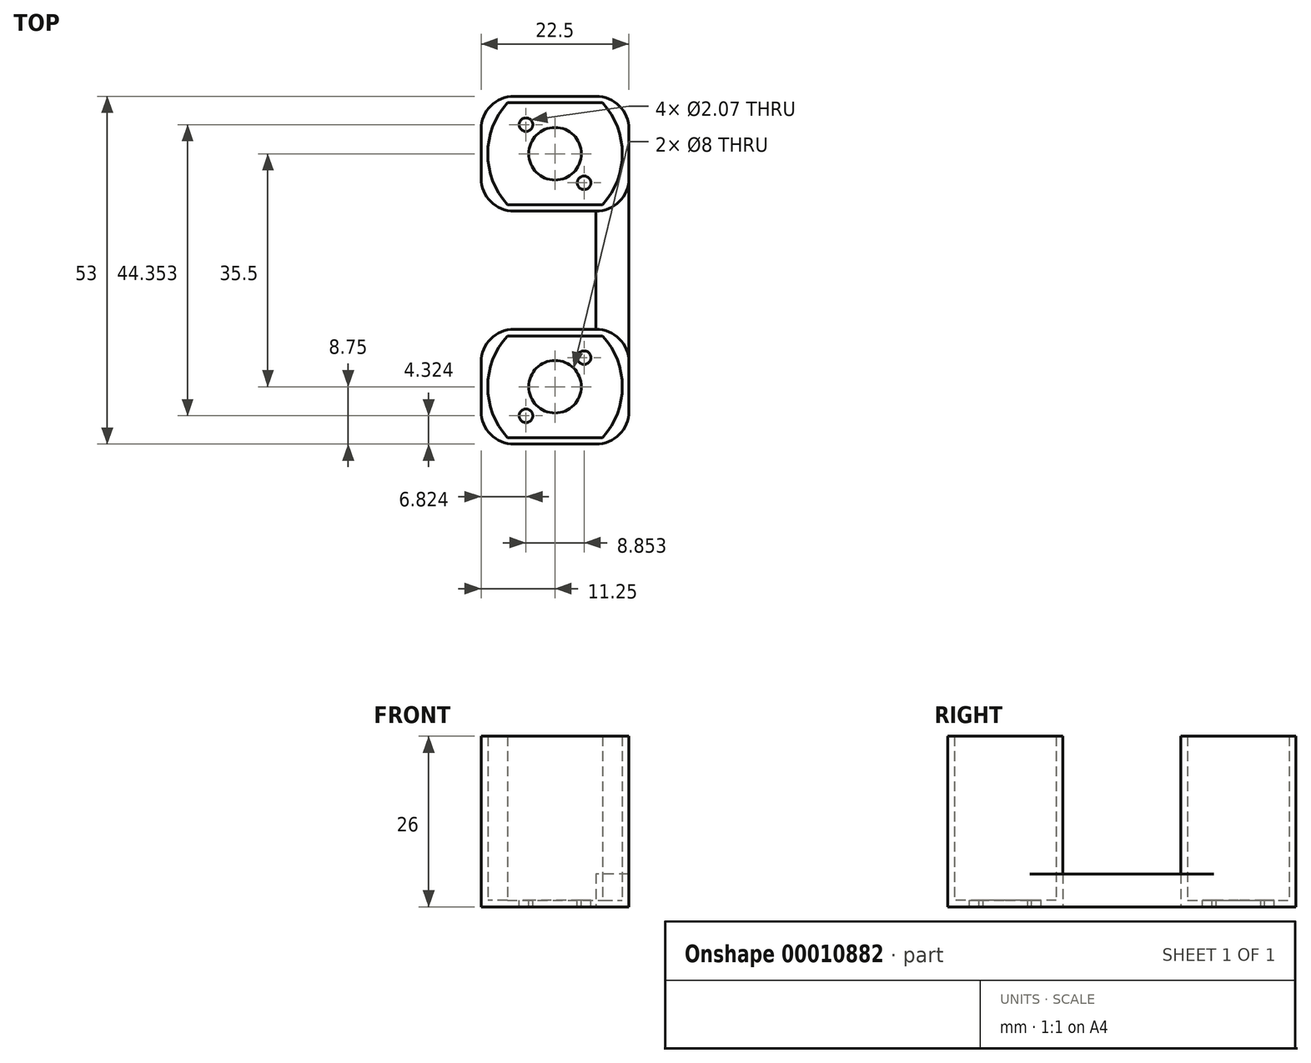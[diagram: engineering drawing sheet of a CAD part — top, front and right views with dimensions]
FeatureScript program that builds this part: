
annotation { "Feature Type Name" : "Feature", "Feature Type Description" : "" }
export const myFeature = defineFeature(function(context is Context, id is Id, definition is map)
    precondition{}
    {
        {
            var Q0;
            Q0=qCreatedBy(makeId("Top.planeOp"),FACE);
            var sketch = newSketch(context, id + "F0", { "sketchPlane" : qUnion([Q0])});
            skLineSegment(sketch, "E0.bottom", {"start": v(-7.25, 7.75) * mm, "end": v(7.25, 7.75) * mm});
            skLineSegment(sketch, "E0.top", {"start": v(-7.25, -7.75) * mm, "end": v(7.25, -7.75) * mm});
            skLineSegment(sketch, "E0.left", {"start": v(-7.25, 7.75) * mm, "end": v(-7.25, -7.75) * mm, "construction": true});
            skLineSegment(sketch, "E0.right", {"start": v(7.25, 7.75) * mm, "end": v(7.25, -7.75) * mm, "construction": true});
            skArc(sketch, "E1", {"start": v(-7.25, 7.75) * mm, "mid": v(-10.25, 0) * mm, "end": v(-7.25, -7.75) * mm});
            skArc(sketch, "E2", {"start": v(7.25, -7.75) * mm, "mid": v(10.25, 0) * mm, "end": v(7.25, 7.75) * mm});
            skLineSegment(sketch, "E3", {"start": v(-7.25, 7.75) * mm, "end": v(-10.25, 7.75) * mm, "construction": true});
            skLineSegment(sketch, "E4", {"start": v(-10.25, 7.75) * mm, "end": v(-10.25, -7.75) * mm, "construction": true});
            skLineSegment(sketch, "E5", {"start": v(-10.25, -7.75) * mm, "end": v(-7.25, -7.75) * mm, "construction": true});
            skLineSegment(sketch, "E6", {"start": v(7.25, -7.75) * mm, "end": v(10.25, -7.75) * mm, "construction": true});
            skLineSegment(sketch, "E7", {"start": v(10.25, -7.75) * mm, "end": v(10.25, 7.75) * mm, "construction": true});
            skLineSegment(sketch, "E8", {"start": v(10.25, 7.75) * mm, "end": v(7.25, 7.75) * mm, "construction": true});
            skLineSegment(sketch, "E9.bottom", {"start": v(-11.25, 8.75) * mm, "end": v(11.25, 8.75) * mm});
            skLineSegment(sketch, "E9.top", {"start": v(-11.25, -8.75) * mm, "end": v(11.25, -8.75) * mm});
            skLineSegment(sketch, "E9.left", {"start": v(-11.25, 8.75) * mm, "end": v(-11.25, -8.75) * mm});
            skLineSegment(sketch, "E9.right", {"start": v(11.25, 8.75) * mm, "end": v(11.25, -8.75) * mm});
            skPoint(sketch, "E10.visualSharp", {"position": v(-11.25, 8.75) * mm});
            skPoint(sketch, "E11.visualSharp", {"position": v(11.25, 8.75) * mm});
            skPoint(sketch, "E12.visualSharp", {"position": v(11.25, -8.75) * mm});
            skPoint(sketch, "E13.visualSharp", {"position": v(-11.25, -8.75) * mm});
            skLineSegment(sketch, "E14", {"start": v(-1.26, 0) * mm, "end": v(1.26, 0) * mm, "construction": true});
            skPoint(sketch, "E15", {"position": v(0, 0) * mm});
            skLineSegment(sketch, "E16", {"start": v(10.25, -7.75) * mm, "end": v(10.25, -8.75) * mm, "construction": true});
            skLineSegment(sketch, "E17", {"start": v(-10.25, 7.75) * mm, "end": v(-10.25, 8.75) * mm, "construction": true});
            skLineSegment(sketch, "E18", {"start": v(-10.25, 7.75) * mm, "end": v(-11.25, 7.75) * mm, "construction": true});
            skLineSegment(sketch, "E19", {"start": v(10.25, -7.75) * mm, "end": v(11.25, -7.75) * mm, "construction": true});
            skSolve(sketch);
        }
        {
            var Q0;
            Q0=qSketchRegion(id+"F0",true);
            extrude(context, id + "F1", {"entities" : qUnion([Q0]), "depth" : 25 * mm});
        }
        {
            var Q0;
            Q0=qCreatedBy(makeId("Top.planeOp"),FACE);
            var sketch = newSketch(context, id + "F2", { "sketchPlane" : qUnion([Q0])});
            skCircle(sketch, "E20", {"center": v(0, 0) * mm, "radius": 4 * mm});
            skLineSegment(sketch, "E21", {"start": v(-4.43, -4.43) * mm, "end": v(4.43, 4.43) * mm, "construction": true});
            skCircle(sketch, "E22", {"center": v(-4.43, -4.43) * mm, "radius": 1.04 * mm});
            skCircle(sketch, "E23", {"center": v(4.43, 4.43) * mm, "radius": 1.04 * mm});
            skLineSegment(sketch, "E24", {"start": v(0, 0) * mm, "end": v(0, -4) * mm, "construction": true});
            skLineSegment(sketch, "E25.bottom", {"start": v(-11.25, -8.75) * mm, "end": v(11.25, -8.75) * mm});
            skLineSegment(sketch, "E25.top", {"start": v(-11.25, 8.75) * mm, "end": v(11.25, 8.75) * mm});
            skLineSegment(sketch, "E25.left", {"start": v(-11.25, -8.75) * mm, "end": v(-11.25, 8.75) * mm});
            skLineSegment(sketch, "E25.right", {"start": v(11.25, -8.75) * mm, "end": v(11.25, 8.75) * mm});
            skSolve(sketch);
        }
        {
            var Q0;
            Q0=qSketchRegion(id+"F2",true);
            extrude(context, id + "F3", {"entities" : qUnion([Q0]), "operationType" : NewBodyOperationType.ADD, "oppositeDirection" : true, "depth" : 1 * mm});
        }
        {
            var Q0;
            Q0=makeQuery(id+"F3.boolean.opBoolean","MERGE",EDGE,{"derivedFrom":[makeQuery(id+"F1.opExtrude","SWEPT_EDGE",EDGE,{"disambiguationData":[OSD([sQuery(id+"F0.wireOp",EDGE,"E9.bottom"),sQuery(id+"F0.wireOp",EDGE,"E9.left")])]}),makeQuery(id+"F3.opExtrude","SWEPT_EDGE",EDGE,{"disambiguationData":[OSD([sQuery(id+"F2.wireOp",EDGE,"E25.top"),sQuery(id+"F2.wireOp",EDGE,"E25.left")])]})]});
            var Q1;
            Q1=makeQuery(id+"F3.boolean.opBoolean","MERGE",EDGE,{"derivedFrom":[makeQuery(id+"F1.opExtrude","SWEPT_EDGE",EDGE,{"disambiguationData":[OSD([sQuery(id+"F0.wireOp",EDGE,"E9.top"),sQuery(id+"F0.wireOp",EDGE,"E9.left")])]}),makeQuery(id+"F3.opExtrude","SWEPT_EDGE",EDGE,{"disambiguationData":[OSD([sQuery(id+"F2.wireOp",EDGE,"E25.bottom"),sQuery(id+"F2.wireOp",EDGE,"E25.left")])]})]});
            var Q2;
            Q2=makeQuery(id+"F3.boolean.opBoolean","MERGE",EDGE,{"derivedFrom":[makeQuery(id+"F1.opExtrude","SWEPT_EDGE",EDGE,{"disambiguationData":[OSD([sQuery(id+"F0.wireOp",EDGE,"E9.top"),sQuery(id+"F0.wireOp",EDGE,"E9.right")])]}),makeQuery(id+"F3.opExtrude","SWEPT_EDGE",EDGE,{"disambiguationData":[OSD([sQuery(id+"F2.wireOp",EDGE,"E25.bottom"),sQuery(id+"F2.wireOp",EDGE,"E25.right")])]})]});
            var Q3;
            Q3=makeQuery(id+"F3.boolean.opBoolean","MERGE",EDGE,{"derivedFrom":[makeQuery(id+"F1.opExtrude","SWEPT_EDGE",EDGE,{"disambiguationData":[OSD([sQuery(id+"F0.wireOp",EDGE,"E9.bottom"),sQuery(id+"F0.wireOp",EDGE,"E9.right")])]}),makeQuery(id+"F3.opExtrude","SWEPT_EDGE",EDGE,{"disambiguationData":[OSD([sQuery(id+"F2.wireOp",EDGE,"E25.top"),sQuery(id+"F2.wireOp",EDGE,"E25.right")])]})]});
            fillet(context, id + "F4", {"entities" : qUnion([Q0, Q1, Q2, Q3]), "radius" : 5 * mm, "tangentPropagation" : true, "allowEdgeOverflow" : false});
        }
        {
            var Q0;
            Q0=makeQuery(id+"F3.opExtrude","CAP_FACE",FACE,{"disambiguationData":[OSD([sQuery(id+"F2.wireOp",EDGE,"E20"),sQuery(id+"F2.wireOp",EDGE,"E22"),sQuery(id+"F2.wireOp",EDGE,"E23"),sQuery(id+"F2.wireOp",EDGE,"E25.bottom"),sQuery(id+"F2.wireOp",EDGE,"E25.top"),sQuery(id+"F2.wireOp",EDGE,"E25.left"),sQuery(id+"F2.wireOp",EDGE,"E25.right")])],"isStart":false});
            var sketch = newSketch(context, id + "F5", { "sketchPlane" : qUnion([Q0])});
            skLineSegment(sketch, "E26.bottom", {"start": v(6.25, -8.75) * mm, "end": v(11.25, -8.75) * mm, "construction": true});
            skLineSegment(sketch, "E26.top", {"start": v(6.25, -17.75) * mm, "end": v(11.25, -17.75) * mm});
            skLineSegment(sketch, "E26.left", {"start": v(6.25, -8.75) * mm, "end": v(6.25, -17.75) * mm});
            skLineSegment(sketch, "E26.right", {"start": v(11.25, -8.75) * mm, "end": v(11.25, -17.75) * mm});
            skArc(sketch, "E27", {"start": v(6.25, -8.75) * mm, "mid": v(9.79, -7.29) * mm, "end": v(11.25, -3.75) * mm});
            skLineSegment(sketch, "E28", {"start": v(11.25, -3.75) * mm, "end": v(11.25, -8.75) * mm});
            skSolve(sketch);
        }
        {
            var Q0;
            Q0 = qSketchRegion(id + "F5", true);
            extrude(context, id + "F6", {"entities" : qUnion([Q0]), "operationType" : NewBodyOperationType.ADD, "oppositeDirection" : true, "depth" : 5 * mm});
        }
        {
            var Q0;
            Q0=makeQuery(id+"F1.opExtrude","SWEPT_BODY",BODY,{"disambiguationData":[OSD([sQuery(id+"F0.wireOp",EDGE,"E0.bottom"),sQuery(id+"F0.wireOp",EDGE,"E0.top"),sQuery(id+"F0.wireOp",EDGE,"E1"),sQuery(id+"F0.wireOp",EDGE,"E2"),sQuery(id+"F0.wireOp",EDGE,"E9.bottom"),sQuery(id+"F0.wireOp",EDGE,"E9.top"),sQuery(id+"F0.wireOp",EDGE,"E9.left"),sQuery(id+"F0.wireOp",EDGE,"E9.right")])]});
            var Q1;
            Q1=makeQuery(id+"F6.opExtrude","SWEPT_FACE",FACE,{"disambiguationData":[OSD([sQuery(id+"F5.wireOp",EDGE,"E26.top")])]});
            mirror(context, id + "F7", {"operationType" : NewBodyOperationType.ADD, "entities" : qUnion([Q0]), "mirrorPlane" : qUnion([Q1])});
        }
    });
